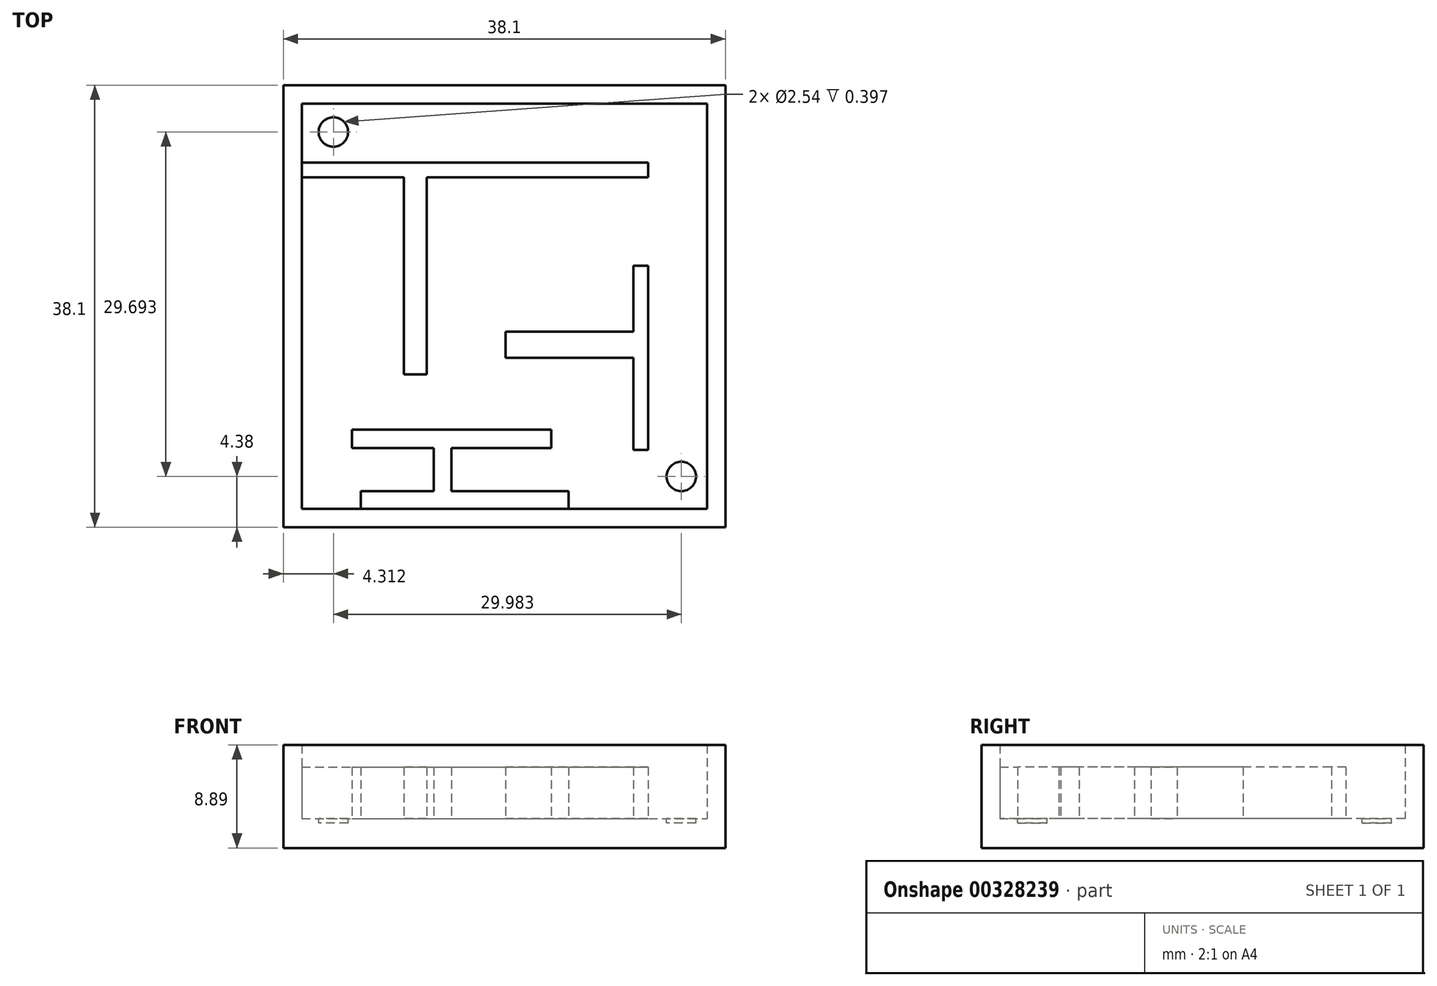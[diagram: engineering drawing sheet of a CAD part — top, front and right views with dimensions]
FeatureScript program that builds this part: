
annotation { "Feature Type Name" : "Feature", "Feature Type Description" : "" }
export const myFeature = defineFeature(function(context is Context, id is Id, definition is map)
    precondition{}
    {
        {
            var Q0;
            Q0=qCreatedBy(makeId("Top.planeOp"),FACE);
            var sketch = newSketch(context, id + "F0", { "sketchPlane" : qUnion([Q0])});
            skLineSegment(sketch, "E0.bottom", {"start": v(-10.18, 20.84) * mm, "end": v(27.92, 20.84) * mm});
            skLineSegment(sketch, "E0.top", {"start": v(-10.18, -17.26) * mm, "end": v(27.92, -17.26) * mm});
            skLineSegment(sketch, "E0.left", {"start": v(-10.18, 20.84) * mm, "end": v(-10.18, -17.26) * mm});
            skLineSegment(sketch, "E0.right", {"start": v(27.92, 20.84) * mm, "end": v(27.92, -17.26) * mm});
            skSolve(sketch);
        }
        {
            var Q0;
            Q0=makeQuery(id+"F0.imprint","IMPRINT",FACE,{"disambiguationData":[TD([[makeQuery(id+"F0.imprint","IMPRINT",EDGE,{"derivedFrom":sQuery(id+"F0.wireOp",EDGE,"E0.bottom")}),-1.0]])]});
            extrude(context, id + "F1", {"entities" : qUnion([Q0]), "depth" : 2.54 * mm});
        }
        {
            var Q0;
            Q0=makeQuery(id+"F1.opExtrude","CAP_FACE",FACE,{"disambiguationData":[OSD([sQuery(id+"F0.wireOp",EDGE,"E0.bottom"),sQuery(id+"F0.wireOp",EDGE,"E0.top"),sQuery(id+"F0.wireOp",EDGE,"E0.left"),sQuery(id+"F0.wireOp",EDGE,"E0.right")])],"isStart":false});
            var sketch = newSketch(context, id + "F2", { "sketchPlane" : qUnion([Q0])});
            skLineSegment(sketch, "E1.0", {"start": v(-8.6, 19.25) * mm, "end": v(26.33, 19.25) * mm});
            skLineSegment(sketch, "E1.1", {"start": v(-8.6, 19.25) * mm, "end": v(-8.6, -15.68) * mm});
            skLineSegment(sketch, "E1.2", {"start": v(-8.6, -15.68) * mm, "end": v(26.33, -15.68) * mm});
            skLineSegment(sketch, "E1.3", {"start": v(26.33, 19.25) * mm, "end": v(26.33, -15.68) * mm});
            skSolve(sketch);
        }
        {
            var Q0;
            Q0=makeQuery(id+"F2.imprint","IMPRINT",FACE,{"disambiguationData":[TD([[makeQuery(id+"F2.imprint","IMPRINT",EDGE,{"derivedFrom":sQuery(id+"F2.wireOp",EDGE,"E1.0")}),1.0]])]});
            extrude(context, id + "F3", {"entities" : qUnion([Q0]), "operationType" : NewBodyOperationType.ADD, "depth" : 6.35 * mm});
        }
        {
            var Q0;
            Q0=makeQuery(id+"F1.opExtrude","CAP_FACE",FACE,{"disambiguationData":[OSD([sQuery(id+"F0.wireOp",EDGE,"E0.bottom"),sQuery(id+"F0.wireOp",EDGE,"E0.top"),sQuery(id+"F0.wireOp",EDGE,"E0.left"),sQuery(id+"F0.wireOp",EDGE,"E0.right")])],"isStart":false});
            var sketch = newSketch(context, id + "F4", { "sketchPlane" : qUnion([Q0])});
            skLineSegment(sketch, "E2.bottom", {"start": v(-8.6, 14.17) * mm, "end": v(21.25, 14.17) * mm});
            skLineSegment(sketch, "E2.top", {"start": v(-8.6, 12.9) * mm, "end": v(0.2, 12.9) * mm});
            skLineSegment(sketch, "E2.left", {"start": v(-8.6, 14.17) * mm, "end": v(-8.6, 12.9) * mm});
            skLineSegment(sketch, "E2.right", {"start": v(21.25, 14.17) * mm, "end": v(21.25, 12.9) * mm});
            skLineSegment(sketch, "E3.bottom", {"start": v(21.25, 5.28) * mm, "end": v(20, 5.28) * mm});
            skLineSegment(sketch, "E3.top", {"start": v(21.25, -10.6) * mm, "end": v(20, -10.6) * mm});
            skLineSegment(sketch, "E3.left", {"start": v(21.25, 5.28) * mm, "end": v(21.25, -10.6) * mm});
            skLineSegment(sketch, "E3.right", {"start": v(20, 5.28) * mm, "end": v(20, -0.4) * mm});
            skLineSegment(sketch, "E4.bottom", {"start": v(20, -2.66) * mm, "end": v(8.97, -2.66) * mm});
            skLineSegment(sketch, "E4.top", {"start": v(20, -0.4) * mm, "end": v(8.97, -0.4) * mm});
            skLineSegment(sketch, "E4.right", {"start": v(8.97, -2.66) * mm, "end": v(8.97, -0.4) * mm});
            skLineSegment(sketch, "E5.trimOffspring", {"start": v(20, -2.66) * mm, "end": v(20, -10.6) * mm});
            skLineSegment(sketch, "E6.top", {"start": v(2.18, -4.07) * mm, "end": v(0.2, -4.07) * mm});
            skLineSegment(sketch, "E6.left", {"start": v(2.18, 12.9) * mm, "end": v(2.18, -4.07) * mm});
            skLineSegment(sketch, "E6.right", {"start": v(0.2, 12.9) * mm, "end": v(0.2, -4.07) * mm});
            skLineSegment(sketch, "E7.trimOffspring", {"start": v(2.18, 12.9) * mm, "end": v(21.25, 12.9) * mm});
            skLineSegment(sketch, "E8.bottom", {"start": v(-3.51, -15.68) * mm, "end": v(14.4, -15.68) * mm});
            skLineSegment(sketch, "E8.top", {"start": v(-3.51, -14.13) * mm, "end": v(2.77, -14.13) * mm});
            skLineSegment(sketch, "E8.left", {"start": v(-3.51, -15.68) * mm, "end": v(-3.51, -14.13) * mm});
            skLineSegment(sketch, "E8.right", {"start": v(14.4, -15.68) * mm, "end": v(14.4, -14.13) * mm});
            skLineSegment(sketch, "E9.bottom", {"start": v(-4.28, -8.83) * mm, "end": v(12.9, -8.83) * mm});
            skLineSegment(sketch, "E9.top", {"start": v(-4.28, -10.42) * mm, "end": v(2.77, -10.42) * mm});
            skLineSegment(sketch, "E9.left", {"start": v(-4.28, -8.83) * mm, "end": v(-4.28, -10.42) * mm});
            skLineSegment(sketch, "E9.right", {"start": v(12.9, -8.83) * mm, "end": v(12.9, -10.42) * mm});
            skLineSegment(sketch, "E10.left", {"start": v(4.31, -10.42) * mm, "end": v(4.31, -14.13) * mm});
            skLineSegment(sketch, "E10.right", {"start": v(2.77, -10.42) * mm, "end": v(2.77, -14.13) * mm});
            skLineSegment(sketch, "E11.trimOffspring", {"start": v(4.31, -10.42) * mm, "end": v(12.9, -10.42) * mm});
            skLineSegment(sketch, "E12.trimOffspring", {"start": v(4.31, -14.13) * mm, "end": v(14.4, -14.13) * mm});
            skCircle(sketch, "E13", {"center": v(-5.87, 16.81) * mm, "radius": 1.27 * mm});
            skCircle(sketch, "E14", {"center": v(24.11, -12.88) * mm, "radius": 1.27 * mm});
            skSolve(sketch);
        }
        {
            var Q0;
            Q0=makeQuery(id+"F4.imprint","IMPRINT",FACE,{"disambiguationData":[TD([[makeQuery(id+"F4.imprint","IMPRINT",EDGE,{"derivedFrom":sQuery(id+"F4.wireOp",EDGE,"E2.bottom")}),-1.0]])]});
            var Q1;
            Q1=makeQuery(id+"F4.imprint","IMPRINT",FACE,{"disambiguationData":[TD([[makeQuery(id+"F4.imprint","IMPRINT",EDGE,{"derivedFrom":sQuery(id+"F4.wireOp",EDGE,"E3.bottom")}),1.0]])]});
            var Q2;
            Q2=makeQuery(id+"F4.imprint","IMPRINT",FACE,{"disambiguationData":[TD([[makeQuery(id+"F4.imprint","IMPRINT",EDGE,{"derivedFrom":sQuery(id+"F4.wireOp",EDGE,"E8.bottom")}),1.0]])]});
            extrude(context, id + "F5", {"entities" : qUnion([Q0, Q1, Q2]), "depth" : 4.44 * mm});
        }
        {
            var Q0;
            Q0=makeQuery(id+"F4.imprint","IMPRINT",FACE,{"disambiguationData":[TD([[makeQuery(id+"F4.imprint","IMPRINT",EDGE,{"derivedFrom":sQuery(id+"F4.wireOp",EDGE,"E14")}),1.0]])]});
            var Q1;
            Q1=makeQuery(id+"F4.imprint","IMPRINT",FACE,{"disambiguationData":[TD([[makeQuery(id+"F4.imprint","IMPRINT",EDGE,{"derivedFrom":sQuery(id+"F4.wireOp",EDGE,"E13")}),1.0]])]});
            extrude(context, id + "F6", {"entities" : qUnion([Q0, Q1]), "operationType" : NewBodyOperationType.REMOVE, "oppositeDirection" : true, "depth" : 0.4 * mm});
        }
    });
